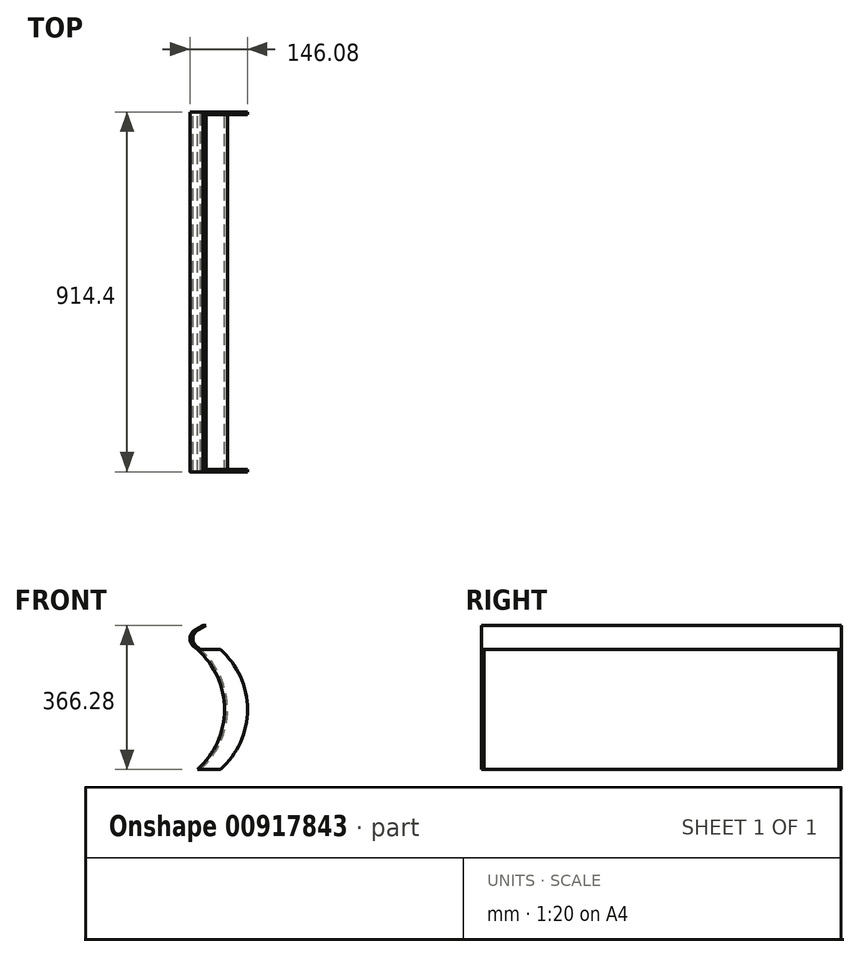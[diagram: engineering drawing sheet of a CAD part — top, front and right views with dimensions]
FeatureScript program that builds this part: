
annotation { "Feature Type Name" : "Feature", "Feature Type Description" : "" }
export const myFeature = defineFeature(function(context is Context, id is Id, definition is map)
    precondition{}
    {
        {
            var Q0;
            Q0=qCreatedBy(makeId("Front.planeOp"),FACE);
            var sketch = newSketch(context, id + "F0", { "sketchPlane" : qUnion([Q0])});
            skArc(sketch, "E0", {"start": v(0, -152.4) * mm, "mid": v(68.8, 0) * mm, "end": v(0, 152.4) * mm});
            skLineSegment(sketch, "E1", {"start": v(0, 152.4) * mm, "end": v(-9.97, 160.93) * mm});
            skLineSegment(sketch, "E2", {"start": v(-6.18, 202.2) * mm, "end": v(13.97, 213.88) * mm});
            skPoint(sketch, "E3.visualSharp", {"position": v(-37.2, 184.24) * mm});
            skArc(sketch, "E3.filletArc", {"start": v(-6.18, 202.2) * mm, "mid": v(-18.74, 182.55) * mm, "end": v(-9.97, 160.93) * mm});
            skArc(sketch, "E4", {"start": v(-7.63, -152.4) * mm, "mid": v(61.16, 0) * mm, "end": v(-7.63, 152.4) * mm});
            skLineSegment(sketch, "E5", {"start": v(-7.63, 152.4) * mm, "end": v(-17.6, 160.93) * mm});
            skLineSegment(sketch, "E6", {"start": v(-13.81, 202.2) * mm, "end": v(6.33, 213.88) * mm});
            skArc(sketch, "E7.filletArc", {"start": v(-13.81, 202.2) * mm, "mid": v(-26.38, 182.55) * mm, "end": v(-17.6, 160.93) * mm});
            skLineSegment(sketch, "E8", {"start": v(6.33, 213.88) * mm, "end": v(13.97, 213.88) * mm});
            skLineSegment(sketch, "E9", {"start": v(-7.63, -152.4) * mm, "end": v(0, -152.4) * mm});
            skSolve(sketch);
        }
        {
            var Q0;
            Q0=makeQuery(id+"F0.imprint","IMPRINT",FACE,{"disambiguationData":[TD([[makeQuery(id+"F0.imprint","IMPRINT",EDGE,{"derivedFrom":sQuery(id+"F0.wireOp",EDGE,"E0")}),1.0]])]});
            extrude(context, id + "F1", {"entities" : qUnion([Q0]), "endBound" : BoundingType.SYMMETRIC, "depth" : 914.4 * mm, "offsetDistance" : 25.4 * mm});
        }
        {
            var Q0;
            Q0=makeQuery(id+"F1.opExtrude","CAP_FACE",FACE,{"disambiguationData":[OSD([sQuery(id+"F0.wireOp",EDGE,"E0"),sQuery(id+"F0.wireOp",EDGE,"E1"),sQuery(id+"F0.wireOp",EDGE,"E2"),sQuery(id+"F0.wireOp",EDGE,"E3.filletArc"),sQuery(id+"F0.wireOp",EDGE,"E4"),sQuery(id+"F0.wireOp",EDGE,"E5"),sQuery(id+"F0.wireOp",EDGE,"E6"),sQuery(id+"F0.wireOp",EDGE,"E7.filletArc"),sQuery(id+"F0.wireOp",EDGE,"E8"),sQuery(id+"F0.wireOp",EDGE,"E9")])],"isStart":false});
            var sketch = newSketch(context, id + "F2", { "sketchPlane" : qUnion([Q0])});
            skLineSegment(sketch, "E10", {"start": v(0, 152.4) * mm, "end": v(50.8, 152.4) * mm});
            skLineSegment(sketch, "E11", {"start": v(0, -152.4) * mm, "end": v(50.8, -152.4) * mm});
            skArc(sketch, "E12", {"start": v(50.8, -152.4) * mm, "mid": v(119.6, 0) * mm, "end": v(50.8, 152.4) * mm});
            skSolve(sketch);
        }
        {
            var Q0;
            Q0=makeQuery(id+"F2.imprint","IMPRINT",FACE,{"disambiguationData":[TD([[makeQuery(id+"F2.imprint","IMPRINT",EDGE,{"derivedFrom":sQuery(id+"F2.wireOp",EDGE,"E10")}),-1.0]])]});
            extrude(context, id + "F3", {"entities" : qUnion([Q0]), "operationType" : NewBodyOperationType.ADD, "oppositeDirection" : true, "depth" : 6.35 * mm, "offsetDistance" : 25.4 * mm});
        }
        {
            var Q0;
            Q0=makeQuery(id+"F1.opExtrude","SWEPT_BODY",BODY,{"disambiguationData":[OSD([sQuery(id+"F0.wireOp",EDGE,"E0"),sQuery(id+"F0.wireOp",EDGE,"E1"),sQuery(id+"F0.wireOp",EDGE,"E2"),sQuery(id+"F0.wireOp",EDGE,"E3.filletArc"),sQuery(id+"F0.wireOp",EDGE,"E4"),sQuery(id+"F0.wireOp",EDGE,"E5"),sQuery(id+"F0.wireOp",EDGE,"E6"),sQuery(id+"F0.wireOp",EDGE,"E7.filletArc"),sQuery(id+"F0.wireOp",EDGE,"E8"),sQuery(id+"F0.wireOp",EDGE,"E9")])]});
            var Q1;
            Q1=qCreatedBy(makeId("Front.planeOp"),FACE);
            mirror(context, id + "F4", {"operationType" : NewBodyOperationType.ADD, "entities" : qUnion([Q0]), "mirrorPlane" : qUnion([Q1])});
        }
    });
